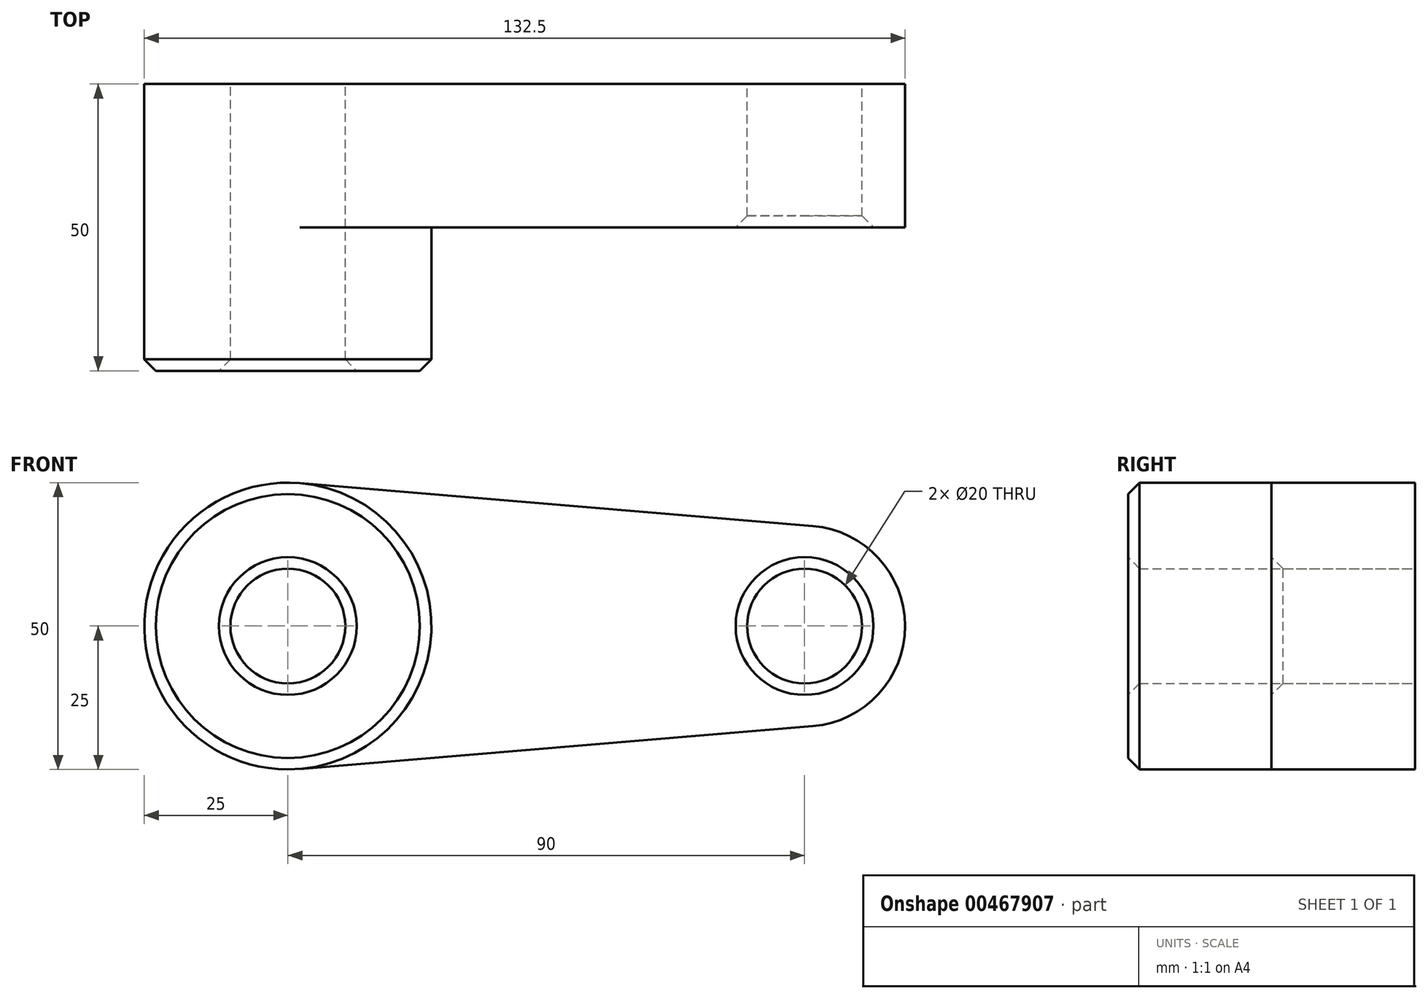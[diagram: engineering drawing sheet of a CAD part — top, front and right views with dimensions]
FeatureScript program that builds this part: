
annotation { "Feature Type Name" : "Feature", "Feature Type Description" : "" }
export const myFeature = defineFeature(function(context is Context, id is Id, definition is map)
    precondition{}
    {
        {
            var Q0;
            Q0=qCreatedBy(makeId("Front.planeOp"),FACE);
            var sketch = newSketch(context, id + "F0", { "sketchPlane" : qUnion([Q0])});
            skCircle(sketch, "E0", {"center": v(0, 0) * mm, "radius": 25 * mm});
            skCircle(sketch, "E1", {"center": v(90, 0) * mm, "radius": 17.5 * mm});
            skLineSegment(sketch, "E2", {"start": v(2.08, 24.91) * mm, "end": v(91.46, 17.44) * mm});
            skLineSegment(sketch, "E3", {"start": v(2.08, -24.91) * mm, "end": v(91.46, -17.44) * mm});
            skCircle(sketch, "E4", {"center": v(0, 0) * mm, "radius": 10 * mm});
            skCircle(sketch, "E5", {"center": v(90, 0) * mm, "radius": 10 * mm});
            skSolve(sketch);
        }
        {
            var Q0;
            Q0=qSketchRegion(id+"F0",true);
            extrude(context, id + "F1", {"entities" : qUnion([Q0]), "depth" : 25 * mm});
        }
        {
            var Q0;
            Q0=makeQuery(id+"F0.imprint","IMPRINT",FACE,{"disambiguationData":[TD([[makeQuery(id+"F0.imprint","IMPRINT",EDGE,{"derivedFrom":sQuery(id+"F0.wireOp",EDGE,"E4")}),-1.0]])]});
            extrude(context, id + "F2", {"entities" : qUnion([Q0]), "operationType" : NewBodyOperationType.ADD, "depth" : 50 * mm});
        }
        {
            var Q0;
            Q0=makeQuery(id+"F2.opExtrude","CAP_EDGE",EDGE,{"disambiguationData":[OSD([sQuery(id+"F0.wireOp",EDGE,"E0")])],"isStart":false});
            var Q1;
            Q1=makeQuery(id+"F2.opExtrude","CAP_EDGE",EDGE,{"disambiguationData":[OSD([sQuery(id+"F0.wireOp",EDGE,"E4")])],"isStart":false});
            var Q2;
            Q2=makeQuery(id+"F1.opExtrude","CAP_EDGE",EDGE,{"disambiguationData":[OSD([sQuery(id+"F0.wireOp",EDGE,"E5")])],"isStart":false});
            chamfer(context, id + "F3", {"entities" : qUnion([Q0, Q1, Q2]), "width" : 2 * mm, "tangentPropagation" : true});
        }
        {
            var Q0;
            Q0=qSketchRegion(id+"F0",true);
            var sketch = newSketch(context, id + "F4", { "sketchPlane" : qUnion([Q0])});
            skSolve(sketch);
        }
        {
            var Q0;
            Q0=sQuery(id+"F0.wireOp",EDGE,"E4");
            extrude(context, id + "F5", {"bodyType" : ToolBodyType.SURFACE, "surfaceEntities" : qUnion([Q0]), "depth" : 25 * mm});
        }
    });
